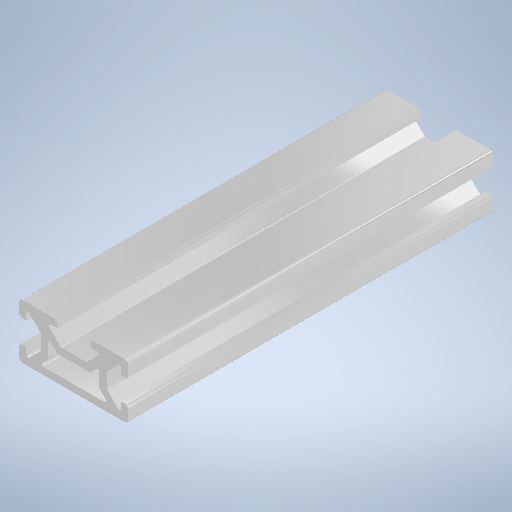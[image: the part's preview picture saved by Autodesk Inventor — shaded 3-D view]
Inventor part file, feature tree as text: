
AUTODESK INVENTOR PART (.ipt)
format: ipt  version: 2025.2 (Build 292293000, 293)  size: 367,104 bytes
history: native  units: mm
features: fillet x2, extrude x1, mirror x1, sketch x1
ambient origin geometry x8: Origin, YZ Plane, XZ Plane, XY Plane, X Axis, Y Axis, Z Axis, Center Point
bodies: Solid1 (feature_tree)
feature tree (5):
  extrude  "Extrusion1"  Depth=6.2mm
  mirror  "Mirror1"
  fillet  "Fillet1"  Radius=15.0mm
  fillet  "Fillet2"  Radius=0.5mm
  sketch  "Sketch1"  dims[d78=15.0mm d87=6.2mm d89=15.0mm d91=0.5mm d92=2.0mm d93=6.0mm d96=45.0deg d97=3.0mm d98=45.0deg d121=2.0mm d122=2.0mm d124=2.0mm d126=2.0mm d127=2.0mm d128=100.0mm d129=0.0mm d130=1.0mm d131=0.5mm]
